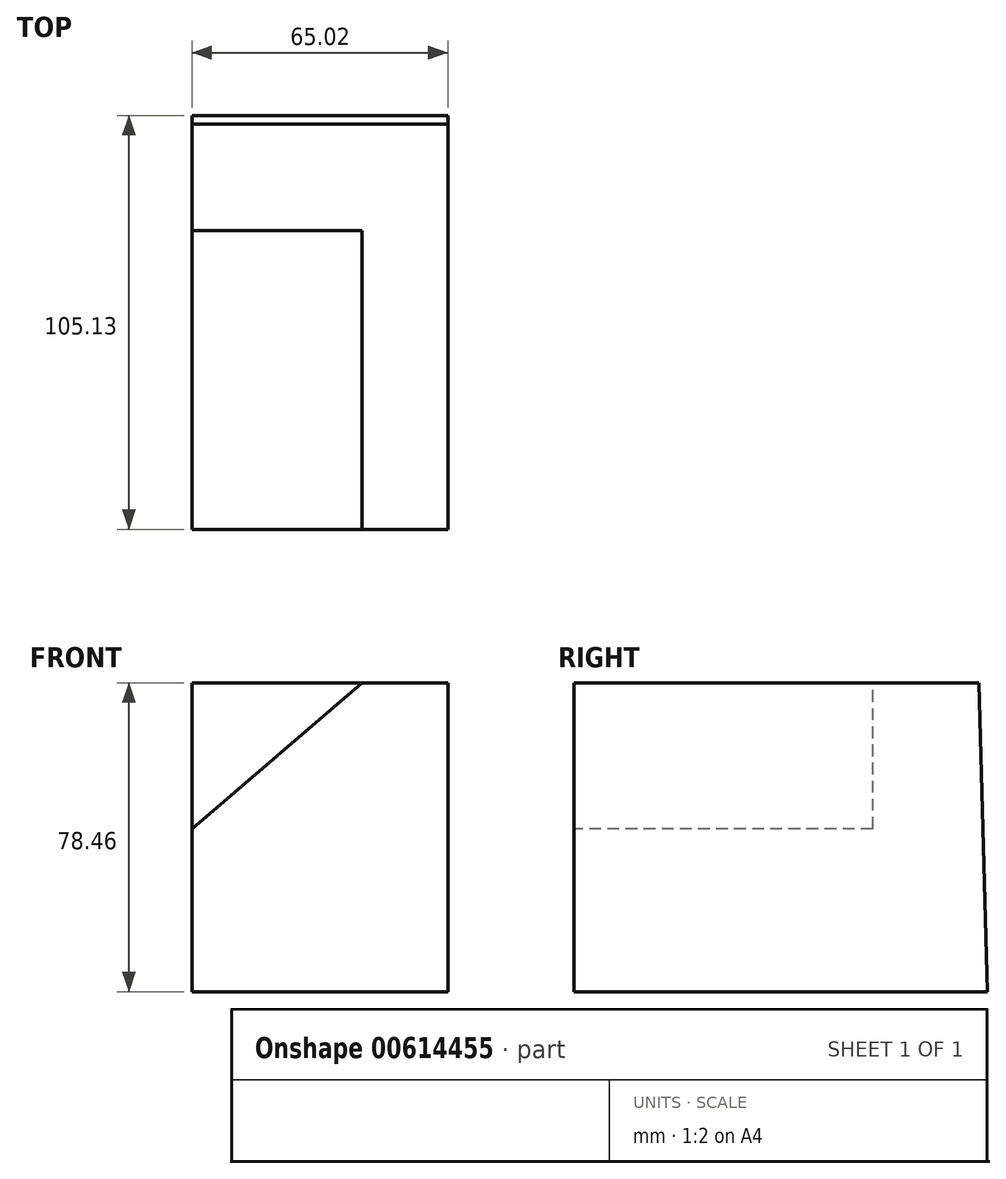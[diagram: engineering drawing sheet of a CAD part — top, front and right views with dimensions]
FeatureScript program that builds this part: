
annotation { "Feature Type Name" : "Feature", "Feature Type Description" : "" }
export const myFeature = defineFeature(function(context is Context, id is Id, definition is map)
    precondition{}
    {
        {
            var Q0;
            Q0=qCreatedBy(makeId("Right.planeOp"),FACE);
            var sketch = newSketch(context, id + "F0", { "sketchPlane" : qUnion([Q0])});
            skLineSegment(sketch, "E0", {"start": v(-56.9, 37.06) * mm, "end": v(46.05, 37.06) * mm});
            skLineSegment(sketch, "E1", {"start": v(46.05, 37.06) * mm, "end": v(48.22, -41.4) * mm});
            skLineSegment(sketch, "E2", {"start": v(48.22, -41.4) * mm, "end": v(-56.9, -41.4) * mm});
            skLineSegment(sketch, "E3", {"start": v(-56.9, -41.4) * mm, "end": v(-56.9, 37.06) * mm});
            skSolve(sketch);
        }
        {
            var Q0;
            Q0 = qSketchRegion(id + "F0", true);
            extrude(context, id + "F1", {"entities" : qUnion([Q0]), "depth" : 65.02 * mm, "offsetDistance" : 25.4 * mm});
        }
        {
            var Q0;
            Q0=makeQuery(id+"F1.opExtrude","SWEPT_FACE",FACE,{"disambiguationData":[OSD([sQuery(id+"F0.wireOp",EDGE,"E3")])]});
            var sketch = newSketch(context, id + "F2", { "sketchPlane" : qUnion([Q0])});
            skLineSegment(sketch, "E4", {"start": v(43.26, 37.06) * mm, "end": v(0, 0) * mm});
            skSolve(sketch);
        }
        {
            var Q0;
            Q0 = qSketchRegion(id + "F2", true);
            var Q1;
            {var subQ0=sQuery(id+"F2.wireOp",EDGE,"E4");Q1=makeQuery(id+"F2.imprint","IMPRINT",FACE,{"disambiguationData":[TD([[makeQuery(id+"F2.imprint","IMPRINT",EDGE,{"derivedFrom":subQ0}),-1.0]])]});}
            extrude(context, id + "F3", {"entities" : qUnion([Q0, Q1]), "operationType" : NewBodyOperationType.REMOVE, "oppositeDirection" : true, "depth" : 75.95 * mm, "offsetDistance" : 25.4 * mm});
        }
    });
